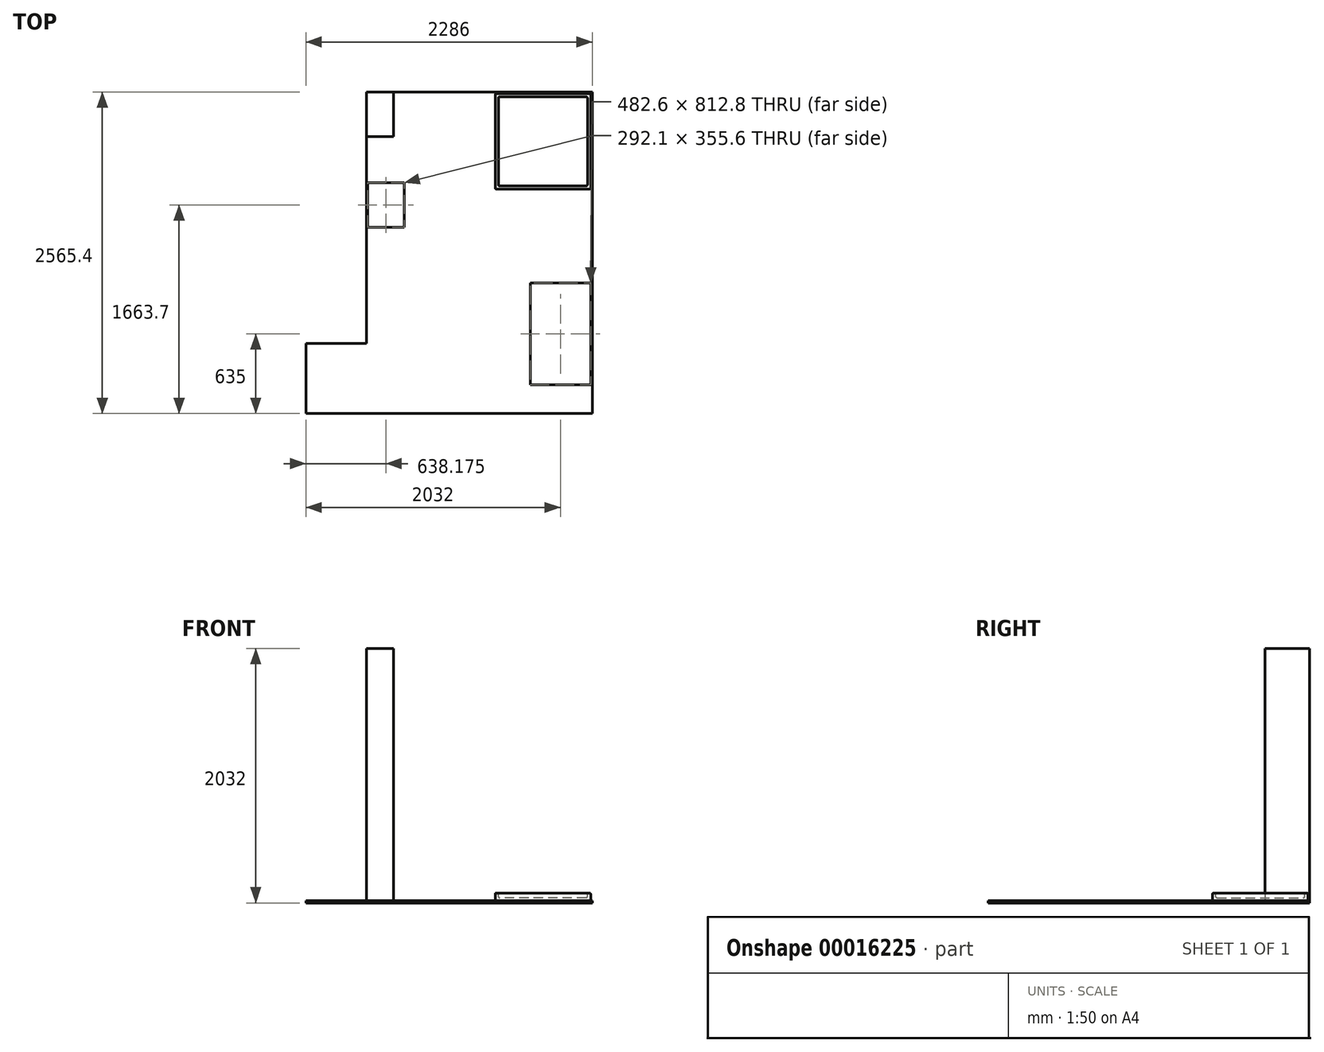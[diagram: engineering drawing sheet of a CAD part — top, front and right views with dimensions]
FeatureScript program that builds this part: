
annotation { "Feature Type Name" : "Feature", "Feature Type Description" : "" }
export const myFeature = defineFeature(function(context is Context, id is Id, definition is map)
    precondition{}
    {
        {
            var Q0;
            Q0=qCreatedBy(makeId("Top.planeOp"),FACE);
            var sketch = newSketch(context, id + "F0", { "sketchPlane" : qUnion([Q0])});
            skLineSegment(sketch, "E0.rect.top", {"start": v(-901.7, 1282.7) * mm, "end": v(901.7, 1282.7) * mm});
            skLineSegment(sketch, "E0.rect.left", {"start": v(-901.7, -723.9) * mm, "end": v(-901.7, 1282.7) * mm});
            skLineSegment(sketch, "E0.rect.right", {"start": v(901.7, -1282.7) * mm, "end": v(901.7, 1282.7) * mm});
            skPoint(sketch, "E0.rect.middle", {"position": v(0, 0) * mm});
            skLineSegment(sketch, "E1.bottom", {"start": v(406.4, -241.3) * mm, "end": v(889, -241.3) * mm});
            skLineSegment(sketch, "E1.top", {"start": v(406.4, -1054.1) * mm, "end": v(889, -1054.1) * mm});
            skLineSegment(sketch, "E1.left", {"start": v(406.4, -241.3) * mm, "end": v(406.4, -1054.1) * mm});
            skLineSegment(sketch, "E1.right", {"start": v(889, -241.3) * mm, "end": v(889, -1054.1) * mm});
            skLineSegment(sketch, "E2", {"start": v(-901.7, -723.9) * mm, "end": v(-1384.3, -723.9) * mm});
            skLineSegment(sketch, "E3", {"start": v(-1384.3, -723.9) * mm, "end": v(-1384.3, -1282.7) * mm});
            skLineSegment(sketch, "E4", {"start": v(-1384.3, -1282.7) * mm, "end": v(901.7, -1282.7) * mm});
            skLineSegment(sketch, "E5.bottom", {"start": v(-685.8, 1282.7) * mm, "end": v(-901.7, 1282.7) * mm});
            skLineSegment(sketch, "E5.top", {"start": v(-685.8, 927.1) * mm, "end": v(-901.7, 927.1) * mm});
            skLineSegment(sketch, "E5.left", {"start": v(-685.8, 1282.7) * mm, "end": v(-685.8, 927.1) * mm});
            skLineSegment(sketch, "E5.right", {"start": v(-901.7, 1282.7) * mm, "end": v(-901.7, 927.1) * mm});
            skLineSegment(sketch, "E6.bottom", {"start": v(-892.18, 558.8) * mm, "end": v(-600.08, 558.8) * mm});
            skLineSegment(sketch, "E6.top", {"start": v(-892.18, 203.2) * mm, "end": v(-600.08, 203.2) * mm});
            skLineSegment(sketch, "E6.left", {"start": v(-892.18, 558.8) * mm, "end": v(-892.18, 203.2) * mm});
            skLineSegment(sketch, "E6.right", {"start": v(-600.08, 558.8) * mm, "end": v(-600.08, 203.2) * mm});
            skSolve(sketch);
        }
        {
            var Q0;
            {var subQ5=sQuery(id+"F0.wireOp",EDGE,"E5.top");var subQ8=makeQuery(id+"F0.imprint","IMPRINT",EDGE,{"derivedFrom":subQ5});var subQ10=sQuery(id+"F0.wireOp",EDGE,"E0.rect.right");Q0=qUnion([makeQuery(id+"F0.imprint","IMPRINT",FACE,{"disambiguationData":[TD([[makeQuery(id+"F0.imprint","IMPRINT",EDGE,{"derivedFrom":subQ10}),1.0]])]}),makeQuery(id+"F0.imprint","IMPRINT",FACE,{"disambiguationData":[TD([[subQ8,-1.0]])]})]);}
            extrude(context, id + "F7", {"entities" : qUnion([Q0]), "depth" : 19.05 * mm});
        }
        {
            var Q0;
            Q0=makeQuery(id+"F7.opExtrude","CAP_FACE",FACE,{"disambiguationData":[OSD([sQuery(id+"F0.wireOp",EDGE,"E0.rect.top"),sQuery(id+"F0.wireOp",EDGE,"E0.rect.left"),sQuery(id+"F0.wireOp",EDGE,"E0.rect.right"),sQuery(id+"F0.wireOp",EDGE,"E1.bottom"),sQuery(id+"F0.wireOp",EDGE,"E1.top"),sQuery(id+"F0.wireOp",EDGE,"E1.left"),sQuery(id+"F0.wireOp",EDGE,"E1.right"),sQuery(id+"F0.wireOp",EDGE,"E2"),sQuery(id+"F0.wireOp",EDGE,"E3"),sQuery(id+"F0.wireOp",EDGE,"E4"),sQuery(id+"F0.wireOp",EDGE,"E6.bottom"),sQuery(id+"F0.wireOp",EDGE,"E6.top"),sQuery(id+"F0.wireOp",EDGE,"E6.left"),sQuery(id+"F0.wireOp",EDGE,"E6.right")])],"isStart":false});
            var sketch = newSketch(context, id + "F1", { "sketchPlane" : qUnion([Q0])});
            skLineSegment(sketch, "E7.left", {"start": v(127, 1270) * mm, "end": v(127, 508) * mm});
            skLineSegment(sketch, "E7.bottom", {"start": v(127, 1270) * mm, "end": v(889, 1270) * mm});
            skLineSegment(sketch, "E7.top", {"start": v(127, 508) * mm, "end": v(889, 508) * mm});
            skLineSegment(sketch, "E7.right", {"start": v(889, 1270) * mm, "end": v(889, 508) * mm});
            skLineSegment(sketch, "E8.0.0", {"start": v(-901.7, 1282.7) * mm, "end": v(-901.7, 1282.7) * mm});
            skLineSegment(sketch, "E8.0.1", {"start": v(-901.7, 1282.7) * mm, "end": v(901.7, 1282.7) * mm});
            skLineSegment(sketch, "E8.0.2", {"start": v(901.7, 1282.7) * mm, "end": v(901.7, 1282.7) * mm});
            skLineSegment(sketch, "E8.0.3", {"start": v(901.7, 1282.7) * mm, "end": v(-901.7, 1282.7) * mm});
            skSolve(sketch);
        }
        {
            var Q0;
            Q0=makeQuery(id+"F1.imprint","IMPRINT",FACE,{"disambiguationData":[TD([[makeQuery(id+"F1.imprint","IMPRINT",EDGE,{"derivedFrom":sQuery(id+"F1.wireOp",EDGE,"E7.left")}),1.0]])]});
            extrude(context, id + "F2", {"entities" : qUnion([Q0]), "depth" : 60.45 * mm});
        }
        {
            var Q0;
            Q0=makeQuery(id+"F2.opExtrude","CAP_FACE",FACE,{"disambiguationData":[OSD([sQuery(id+"F1.wireOp",EDGE,"E7.left"),sQuery(id+"F1.wireOp",EDGE,"E7.bottom"),sQuery(id+"F1.wireOp",EDGE,"E7.top"),sQuery(id+"F1.wireOp",EDGE,"E7.right")])],"isStart":false});
            var sketch = newSketch(context, id + "F3", { "sketchPlane" : qUnion([Q0])});
            skLineSegment(sketch, "E9.0.0", {"start": v(889, 1270) * mm, "end": v(127, 1270) * mm});
            skLineSegment(sketch, "E9.0.1", {"start": v(127, 1270) * mm, "end": v(127, 508) * mm});
            skLineSegment(sketch, "E9.0.2", {"start": v(127, 508) * mm, "end": v(889, 508) * mm});
            skLineSegment(sketch, "E9.0.3", {"start": v(889, 508) * mm, "end": v(889, 1270) * mm});
            skLineSegment(sketch, "E10", {"start": v(152.4, 1244.6) * mm, "end": v(863.6, 1244.6) * mm});
            skLineSegment(sketch, "E11", {"start": v(863.6, 1244.6) * mm, "end": v(863.6, 533.4) * mm});
            skLineSegment(sketch, "E12", {"start": v(863.6, 533.4) * mm, "end": v(152.4, 533.4) * mm});
            skLineSegment(sketch, "E13", {"start": v(152.4, 533.4) * mm, "end": v(152.4, 1244.6) * mm});
            skSolve(sketch);
        }
        {
            var Q0;
            Q0=makeQuery(id+"F3.imprint","IMPRINT",FACE,{"disambiguationData":[TD([[makeQuery(id+"F3.imprint","IMPRINT",EDGE,{"derivedFrom":sQuery(id+"F3.wireOp",EDGE,"E10")}),-1.0]])]});
            extrude(context, id + "F4", {"entities" : qUnion([Q0]), "operationType" : NewBodyOperationType.REMOVE, "oppositeDirection" : true, "depth" : 38.1 * mm});
        }
        {
            var Q0;
            Q0=makeQuery(id+"F4.boolean.opBoolean","COPY",FACE,{"derivedFrom":makeQuery(id+"F4.opExtrude","SWEPT_FACE",FACE,{"disambiguationData":[OSD([sQuery(id+"F3.wireOp",EDGE,"E10")])]})});
            var Q1;
            Q1=makeQuery(id+"F4.boolean.opBoolean","COPY",FACE,{"derivedFrom":makeQuery(id+"F4.opExtrude","SWEPT_FACE",FACE,{"disambiguationData":[OSD([sQuery(id+"F3.wireOp",EDGE,"E12")])]})});
            var Q2;
            Q2=makeQuery(id+"F4.boolean.opBoolean","COPY",FACE,{"derivedFrom":makeQuery(id+"F4.opExtrude","SWEPT_FACE",FACE,{"disambiguationData":[OSD([sQuery(id+"F3.wireOp",EDGE,"E11")])]})});
            var Q3;
            Q3=makeQuery(id+"F4.boolean.opBoolean","COPY",FACE,{"derivedFrom":makeQuery(id+"F4.opExtrude","SWEPT_FACE",FACE,{"disambiguationData":[OSD([sQuery(id+"F3.wireOp",EDGE,"E13")])]})});
            var Q4;
            Q4=makeQuery(id+"F2.opExtrude","SWEPT_FACE",FACE,{"disambiguationData":[OSD([sQuery(id+"F1.wireOp",EDGE,"E7.top")])]});
            var Q5;
            Q5=makeQuery(id+"F2.opExtrude","SWEPT_FACE",FACE,{"disambiguationData":[OSD([sQuery(id+"F1.wireOp",EDGE,"E7.right")])]});
            var Q6;
            Q6=makeQuery(id+"F2.opExtrude","SWEPT_FACE",FACE,{"disambiguationData":[OSD([sQuery(id+"F1.wireOp",EDGE,"E7.bottom")])]});
            var Q7;
            Q7=makeQuery(id+"F2.opExtrude","SWEPT_FACE",FACE,{"disambiguationData":[OSD([sQuery(id+"F1.wireOp",EDGE,"E7.left")])]});
            fillet(context, id + "F5", {"entities" : qUnion([Q0, Q1, Q2, Q3, Q4, Q5, Q6, Q7]), "radius" : 9.65 * mm, "tangentPropagation" : true, "allowEdgeOverflow" : false});
        }
        {
            var Q0;
            {var subQ4=sQuery(id+"F0.wireOp",EDGE,"E5.top");Q0=makeQuery(id+"F0.imprint","IMPRINT",FACE,{"disambiguationData":[TD([[makeQuery(id+"F0.imprint","IMPRINT",EDGE,{"derivedFrom":subQ4}),-1.0]])]});}
            extrude(context, id + "F6", {"entities" : qUnion([Q0]), "operationType" : NewBodyOperationType.ADD, "depth" : 2032 * mm});
        }
    });
